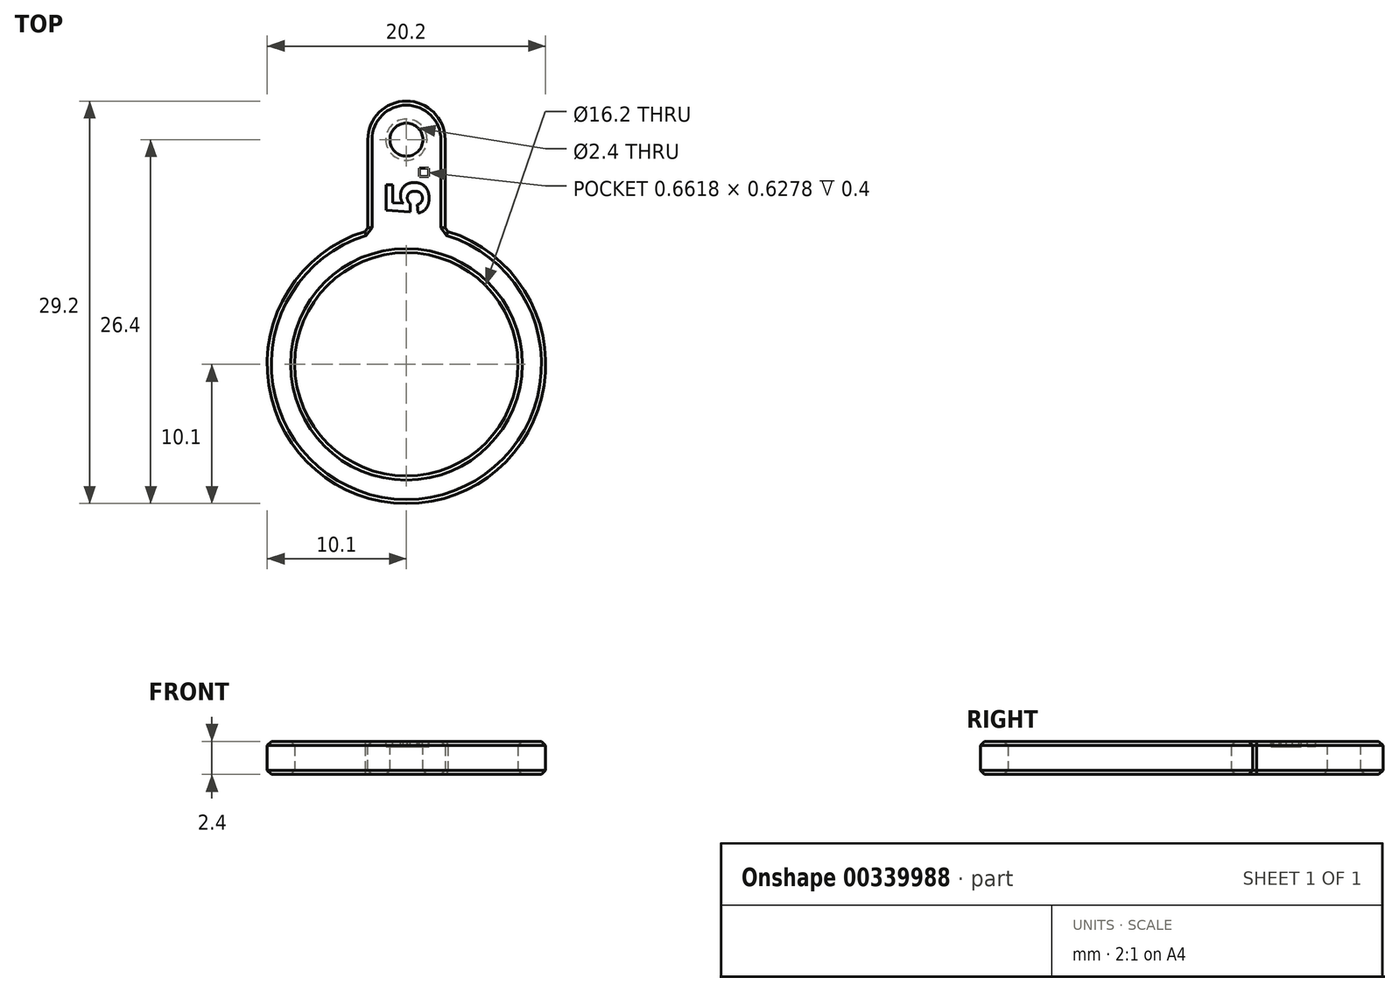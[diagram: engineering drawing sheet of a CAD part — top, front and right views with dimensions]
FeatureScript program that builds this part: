
annotation { "Feature Type Name" : "Feature", "Feature Type Description" : "" }
export const myFeature = defineFeature(function(context is Context, id is Id, definition is map)
    precondition{}
    {
        {
            var Q0;
            Q0=qCreatedBy(makeId("Top.planeOp"),FACE);
            var sketch = newSketch(context, id + "F0", { "sketchPlane" : qUnion([Q0])});
            skCircle(sketch, "E0", {"center": v(0, 0) * mm, "radius": 8.1 * mm});
            skCircle(sketch, "E1", {"center": v(0, 0) * mm, "radius": 10.1 * mm});
            skLineSegment(sketch, "E2.bottom", {"start": v(2.8, 1.1) * mm, "end": v(-2.8, 1.1) * mm});
            skLineSegment(sketch, "E2.top", {"start": v(2.8, 19.1) * mm, "end": v(-2.8, 19.1) * mm});
            skLineSegment(sketch, "E2.left", {"start": v(2.8, 1.1) * mm, "end": v(2.8, 19.1) * mm});
            skLineSegment(sketch, "E2.right", {"start": v(-2.8, 1.1) * mm, "end": v(-2.8, 19.1) * mm});
            skPoint(sketch, "E2.middle", {"position": v(0, 10.1) * mm});
            skSolve(sketch);
        }
        {
            var Q0;
            Q0=qSketchRegion(id+"F0",true);
            extrude(context, id + "F1", {"entities" : qUnion([Q0]), "depth" : 2.4 * mm});
        }
        {
            var Q0;
            Q0=makeQuery(id+"F1.opExtrude","SWEPT_EDGE",EDGE,{"disambiguationData":[OSD([sQuery(id+"F0.wireOp",EDGE,"E2.top"),sQuery(id+"F0.wireOp",EDGE,"E2.right")])]});
            var Q1;
            Q1=makeQuery(id+"F1.opExtrude","SWEPT_EDGE",EDGE,{"disambiguationData":[OSD([sQuery(id+"F0.wireOp",EDGE,"E2.top"),sQuery(id+"F0.wireOp",EDGE,"E2.left")])]});
            fillet(context, id + "F2", {"entities" : qUnion([Q0, Q1]), "radius" : 2.8 * mm, "tangentPropagation" : true, "allowEdgeOverflow" : false});
        }
        {
            var Q0;
            Q0=makeQuery(id+"F1.opExtrude","CAP_FACE",FACE,{"disambiguationData":[OSD([sQuery(id+"F0.wireOp",EDGE,"E0"),sQuery(id+"F0.wireOp",EDGE,"E1"),sQuery(id+"F0.wireOp",EDGE,"E2.top"),sQuery(id+"F0.wireOp",EDGE,"E2.left"),sQuery(id+"F0.wireOp",EDGE,"E2.right")])],"isStart":false});
            var sketch = newSketch(context, id + "F3", { "sketchPlane" : qUnion([Q0])});
            skCircle(sketch, "E3", {"center": v(0, 16.3) * mm, "radius": 1.2 * mm});
            skSolve(sketch);
        }
        {
            var Q0;
            Q0=qSketchRegion(id+"F3",true);
            extrude(context, id + "F4", {"entities" : qUnion([Q0]), "operationType" : NewBodyOperationType.REMOVE, "oppositeDirection" : true, "depth" : 25 * mm});
        }
        {
            var Q0;
            Q0=makeQuery(id+"F4.boolean.opBoolean","COPY",EDGE,{"derivedFrom":makeQuery(id+"F4.opExtrude","CAP_EDGE",EDGE,{"disambiguationData":[OSD([sQuery(id+"F3.wireOp",EDGE,"E3")])],"isStart":true})});
            var Q1;
            Q1=makeQuery(id+"F4.boolean.opBoolean","INTERSECT",EDGE,{"derivedFrom":[makeQuery(id+"F1.opExtrude","CAP_FACE",FACE,{"disambiguationData":[OSD([sQuery(id+"F0.wireOp",EDGE,"E0"),sQuery(id+"F0.wireOp",EDGE,"E1"),sQuery(id+"F0.wireOp",EDGE,"E2.top"),sQuery(id+"F0.wireOp",EDGE,"E2.left"),sQuery(id+"F0.wireOp",EDGE,"E2.right")])],"isStart":true}),makeQuery(id+"F4.opExtrude","SWEPT_FACE",FACE,{"disambiguationData":[OSD([sQuery(id+"F3.wireOp",EDGE,"E3")])]})]});
            var Q2;
            {var subQ0=sQuery(id+"F0.wireOp",EDGE,"E2.right");var subQ1=sQuery(id+"F0.wireOp",EDGE,"E2.top");Q2=makeQuery(id+"F2.opFillet","BLEND_EDGE",EDGE,{"blendedFrom":[makeQuery(id+"F1.opExtrude","SWEPT_EDGE",EDGE,{"disambiguationData":[OSD([subQ1,subQ0])]}),makeQuery(id+"F1.opExtrude","CAP_FACE",FACE,{"disambiguationData":[OSD([sQuery(id+"F0.wireOp",EDGE,"E0"),sQuery(id+"F0.wireOp",EDGE,"E1"),subQ1,sQuery(id+"F0.wireOp",EDGE,"E2.left"),subQ0])],"isStart":true})],"blendedInto":[makeQuery(id+"F1.opExtrude","CAP_FACE",FACE,{"disambiguationData":[OSD([sQuery(id+"F0.wireOp",EDGE,"E0"),sQuery(id+"F0.wireOp",EDGE,"E1"),subQ1,sQuery(id+"F0.wireOp",EDGE,"E2.left"),subQ0])],"isStart":true})]});}
            var Q3;
            {var subQ0=sQuery(id+"F0.wireOp",EDGE,"E2.right");var subQ1=sQuery(id+"F0.wireOp",EDGE,"E2.top");Q3=makeQuery(id+"F2.opFillet","BLEND_EDGE",EDGE,{"blendedFrom":[makeQuery(id+"F1.opExtrude","SWEPT_EDGE",EDGE,{"disambiguationData":[OSD([subQ1,subQ0])]}),makeQuery(id+"F1.opExtrude","CAP_FACE",FACE,{"disambiguationData":[OSD([sQuery(id+"F0.wireOp",EDGE,"E0"),sQuery(id+"F0.wireOp",EDGE,"E1"),subQ1,sQuery(id+"F0.wireOp",EDGE,"E2.left"),subQ0])],"isStart":false})],"blendedInto":[makeQuery(id+"F1.opExtrude","CAP_FACE",FACE,{"disambiguationData":[OSD([sQuery(id+"F0.wireOp",EDGE,"E0"),sQuery(id+"F0.wireOp",EDGE,"E1"),subQ1,sQuery(id+"F0.wireOp",EDGE,"E2.left"),subQ0])],"isStart":false})]});}
            var Q4;
            Q4=makeQuery(id+"F1.opExtrude","CAP_EDGE",EDGE,{"disambiguationData":[OSD([sQuery(id+"F0.wireOp",EDGE,"E1")])],"isStart":false});
            var Q5;
            Q5=makeQuery(id+"F1.opExtrude","CAP_EDGE",EDGE,{"disambiguationData":[OSD([sQuery(id+"F0.wireOp",EDGE,"E1")])],"isStart":true});
            var Q6;
            Q6=makeQuery(id+"F1.opExtrude","SWEPT_EDGE",EDGE,{"disambiguationData":[OSD([sQuery(id+"F0.wireOp",EDGE,"E1"),sQuery(id+"F0.wireOp",EDGE,"E2.left")])]});
            var Q7;
            Q7=makeQuery(id+"F1.opExtrude","SWEPT_EDGE",EDGE,{"disambiguationData":[OSD([sQuery(id+"F0.wireOp",EDGE,"E1"),sQuery(id+"F0.wireOp",EDGE,"E2.right")])]});
            var Q8;
            Q8=makeQuery(id+"F1.opExtrude","CAP_EDGE",EDGE,{"disambiguationData":[OSD([sQuery(id+"F0.wireOp",EDGE,"E0")])],"isStart":true});
            var Q9;
            Q9=makeQuery(id+"F1.opExtrude","CAP_EDGE",EDGE,{"disambiguationData":[OSD([sQuery(id+"F0.wireOp",EDGE,"E0")])],"isStart":false});
            chamfer(context, id + "F5", {"entities" : qUnion([Q0, Q1, Q2, Q3, Q4, Q5, Q6, Q7, Q8, Q9]), "width" : 0.3 * mm, "tangentPropagation" : true});
        }
        {
            var Q0;
            Q0=makeQuery(id+"F1.opExtrude","CAP_FACE",FACE,{"disambiguationData":[OSD([sQuery(id+"F0.wireOp",EDGE,"E0"),sQuery(id+"F0.wireOp",EDGE,"E1"),sQuery(id+"F0.wireOp",EDGE,"E2.top"),sQuery(id+"F0.wireOp",EDGE,"E2.left"),sQuery(id+"F0.wireOp",EDGE,"E2.right")])],"isStart":false});
            var sketch = newSketch(context, id + "F6", { "sketchPlane" : qUnion([Q0])});
            skText(sketch, "E4", { "text": "5.", "fontName": "Arimo-Bold.ttf"});
            skLineSegment(sketch, "E5", {"start": v(0, 11.1) * mm, "end": v(0, 0) * mm});
            skPoint(sketch, "E5.endSnap0", {"position": v(0, 11.1) * mm});
            const initialGuessF6  = {"E4": [0.0016, 0.01084, 0, 1, 0.0032]};
            skSetInitialGuess(sketch, initialGuessF6);
            skSolve(sketch);
        }
        {
            var Q0;
            Q0=qSketchRegion(id+"F6",true);
            extrude(context, id + "F7", {"entities" : qUnion([Q0]), "operationType" : NewBodyOperationType.REMOVE, "oppositeDirection" : true, "depth" : 0.4 * mm});
        }
    });
